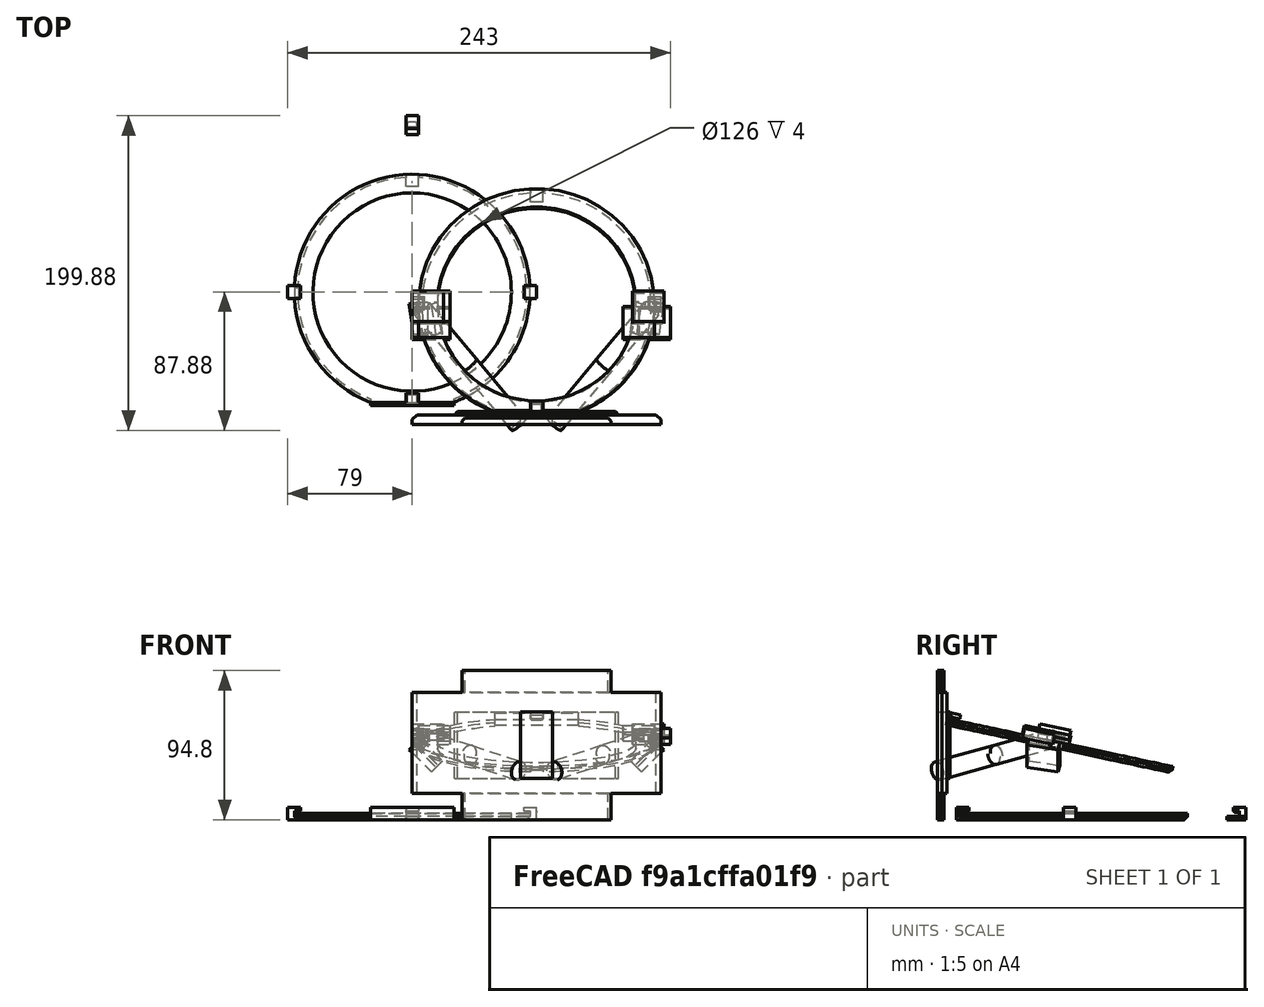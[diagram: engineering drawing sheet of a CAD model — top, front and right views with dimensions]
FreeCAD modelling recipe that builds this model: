
FCSTD DOCUMENT  (FreeCAD 0.19R0.19.2)
Label: waferHolder_024
License: All rights reserved
LicenseURL: http://en.wikipedia.org/wiki/All_rights_reserved
objects: Part::Box×55, Part::Chamfer×36, Part::MultiFuse×21, Part::Cylinder×16, Part::Cut×14, Sketcher::SketchObject×9, Part::Extrusion×9, Part::Fuse×4, Part::Mirroring×2, App::MeasureDistance×1
note: 166 computed .brp shape members not serialized (recipe doc carries the construction recipe); baked Part::Feature solids carry a one-line shape summary decoded from their .brp

FEATURE [Part::Box] Box003  label="bitHolderTop"
  AttacherType = Attacher::AttachEngine3D
  Height = 2
  Length = 8
  Placement = pos=(-4,100,0) rot=(0,0,1;0rad)
  Width = 12
FEATURE [Part::Box] Box008  label="holderBitLeft003"
  AttacherType = Attacher::AttachEngine3D
  Height = 2
  Length = 8
  Placement = pos=(-4,71,2) rot=(0,0,1;0rad)
  Width = 8
FEATURE [Part::Box] Box009  label="bitHolderTopCutout001"
  AttacherType = Attacher::AttachEngine3D
  Height = 4
  Length = 8
  Placement = pos=(-4,67,-2) rot=(0,0,1;0rad)
  Width = 12
FEATURE [Sketcher::SketchObject] Sketch002
  FullyConstrained = true
  sketch-geometry (3):
    g0: Circle CenterX=-3.1415e-12 CenterY=5.6243e-12 CenterZ=0 NormalX=0 NormalY=0 NormalZ=1 AngleXU=0 Radius=63
    g1: ArcOfCircle CenterX=-3.1415e-12 CenterY=5.6243e-12 CenterZ=0 NormalX=0 NormalY=0 NormalZ=1 AngleXU=0 Radius=74.8482 StartAngle=5.07429 EndAngle=10.6337
    g2: LineSegment StartX=-26.5 StartY=-70.0001 StartZ=0 EndX=26.5 EndY=-70.0001 EndZ=0
  constraints (6):
    c: Block(g0)
    c: Coincident(g1,g0)
    c: Block(g1)
    c: Coincident(g2,g1)
    c: Coincident(g2,g1)
    c: Horizontal(g2)
FEATURE [Part::Extrusion] Extrude002  label="mainHolderRing003"
  Base = -> Sketch002
  Dir = (0,0,1)
  DirMode = 2
  FaceMakerClass = Part::FaceMakerBullseye
  LengthFwd = 4
  LengthRev = 0
  Solid = true
  Symmetric = false
FEATURE [Part::Chamfer] Chamfer001
  Base = -> Extrude002
  Edges = 1 edges r=2: [Edge3]
FEATURE [Part::Cut] Cut002  label="mainHolderRing004"
  Base = -> Chamfer001
  Tool = -> Box009
FEATURE [Part::Cut] Cut003  label="bitHolderTop001"
  Base = -> Box008
  Tool = -> Cut002
FEATURE [Part::Box] Box010  label="holderBitLeft004"
  AttacherType = Attacher::AttachEngine3D
  Height = 2
  Length = 8
  Placement = pos=(-4,71,2) rot=(0,0,1;0rad)
  Width = 8
FEATURE [Part::Box] Box011  label="bitHolderTopCutout002"
  AttacherType = Attacher::AttachEngine3D
  Height = 4
  Length = 8
  Placement = pos=(-4,67,-2) rot=(0,0,1;0rad)
  Width = 12
FEATURE [Sketcher::SketchObject] Sketch003
  FullyConstrained = true
  sketch-geometry (3):
    g0: Circle CenterX=-3.1415e-12 CenterY=5.6243e-12 CenterZ=0 NormalX=0 NormalY=0 NormalZ=1 AngleXU=0 Radius=63
    g1: ArcOfCircle CenterX=-3.1415e-12 CenterY=5.6243e-12 CenterZ=0 NormalX=0 NormalY=0 NormalZ=1 AngleXU=0 Radius=74.8482 StartAngle=5.07429 EndAngle=10.6337
    g2: LineSegment StartX=-26.5 StartY=-70.0001 StartZ=0 EndX=26.5 EndY=-70.0001 EndZ=0
  constraints (6):
    c: Block(g0)
    c: Coincident(g1,g0)
    c: Block(g1)
    c: Coincident(g2,g1)
    c: Coincident(g2,g1)
    c: Horizontal(g2)
FEATURE [Part::Extrusion] Extrude003  label="mainHolderRing006"
  Base = -> Sketch003
  Dir = (0,0,1)
  DirMode = 2
  FaceMakerClass = Part::FaceMakerBullseye
  LengthFwd = 4
  LengthRev = 0
  Solid = true
  Symmetric = false
FEATURE [Part::Chamfer] Chamfer002
  Base = -> Extrude003
  Edges = 1 edges r=2: [Edge3]
FEATURE [Part::Cut] Cut005  label="mainHolderRing005"
  Base = -> Chamfer002
  Tool = -> Box011
FEATURE [Part::Cut] Cut004  label="bitHolderTop002"
  Base = -> Box010
  Placement = pos=(0,0,2) rot=(0,0,1;0rad)
  Tool = -> Cut005
FEATURE [Part::Box] Box012  label="holderBitLeft005"
  AttacherType = Attacher::AttachEngine3D
  Height = 2
  Length = 8
  Placement = pos=(-4,71,2) rot=(0,0,1;0rad)
  Width = 8
FEATURE [Part::Box] Box013  label="bitHolderTopCutout003"
  AttacherType = Attacher::AttachEngine3D
  Height = 4
  Length = 8
  Placement = pos=(-4,67,-2) rot=(0,0,1;0rad)
  Width = 12
FEATURE [Sketcher::SketchObject] Sketch004
  FullyConstrained = true
  sketch-geometry (3):
    g0: Circle CenterX=-3.1415e-12 CenterY=5.6243e-12 CenterZ=0 NormalX=0 NormalY=0 NormalZ=1 AngleXU=0 Radius=63
    g1: ArcOfCircle CenterX=-3.1415e-12 CenterY=5.6243e-12 CenterZ=0 NormalX=0 NormalY=0 NormalZ=1 AngleXU=0 Radius=74.8482 StartAngle=5.07429 EndAngle=10.6337
    g2: LineSegment StartX=-26.5 StartY=-70.0001 StartZ=0 EndX=26.5 EndY=-70.0001 EndZ=0
  constraints (6):
    c: Block(g0)
    c: Coincident(g1,g0)
    c: Block(g1)
    c: Coincident(g2,g1)
    c: Coincident(g2,g1)
    c: Horizontal(g2)
FEATURE [Part::Extrusion] Extrude004  label="mainHolderRing008"
  Base = -> Sketch004
  Dir = (0,0,1)
  DirMode = 2
  FaceMakerClass = Part::FaceMakerBullseye
  LengthFwd = 4
  LengthRev = 0
  Solid = true
  Symmetric = false
FEATURE [Part::Chamfer] Chamfer003
  Base = -> Extrude004
  Edges = 1 edges r=2: [Edge3]
FEATURE [Part::Cut] Cut007  label="mainHolderRing007"
  Base = -> Chamfer003
  Tool = -> Box013
FEATURE [Part::Cut] Cut006  label="bitHolderTop003"
  Base = -> Box012
  Placement = pos=(0,0,4) rot=(0,0,1;0rad)
  Tool = -> Cut007
FEATURE [Part::Box] Box014  label="bitHoldertop006"
  AttacherType = Attacher::AttachEngine3D
  Height = 3.4
  Length = 8
  Placement = pos=(-4,71,4.6) rot=(0,0,1;0rad)
  Width = 8
FEATURE [Part::MultiFuse] Fusion001  label="holderTop"
  Placement = pos=(0,33,0) rot=(0,0,1;0rad)
  Shapes = -> [Cut003,Cut004,Cut006,Box014]
FEATURE [Part::Chamfer] Chamfer004
  Base = -> Fusion001
  Edges = 1 edges r=1: [Edge16]
FEATURE [Part::Chamfer] Chamfer009
  Base = -> Chamfer004
  Edges = 1 edges r=1: [Edge1]
FEATURE [Part::Chamfer] Chamfer010
  Base = -> Chamfer009
  Edges = 1 edges r=1: [Edge32]
FEATURE [Part::Box] Box018  label="base001"
  AttacherType = Attacher::AttachEngine3D
  Height = 64.44
  Length = 158
  Placement = pos=(0,-84,16.6) rot=(0,0,1;0rad)
  Width = 6
FEATURE [Part::Box] Box019  label="base002"
  AttacherType = Attacher::AttachEngine3D
  Height = 94.8
  Length = 94.8
  Placement = pos=(31.6,-84,0) rot=(0,0,1;0rad)
  Width = 4
FEATURE [Part::Box] Box020  label="base003"
  AttacherType = Attacher::AttachEngine3D
  Height = 42.44
  Length = 104.28
  Placement = pos=(26.86,-84,26.18) rot=(0,0,1;0rad)
  Width = 8
FEATURE [Part::Chamfer] Chamfer014
  Base = -> Box018
  Edges = 1 edges r=3: [Edge3]
FEATURE [Part::Chamfer] Chamfer015
  Base = -> Chamfer014
  Edges = 1 edges r=3: [Edge15]
FEATURE [Part::Chamfer] Chamfer016
  Base = -> Box019
  Edges = 1 edges r=2: [Edge3]
FEATURE [Part::Chamfer] Chamfer017
  Base = -> Box020
  Edges = 1 edges r=2: [Edge3]
FEATURE [Part::Chamfer] Chamfer018
  Base = -> Chamfer016
  Edges = 1 edges r=2: [Edge15]
FEATURE [Part::Chamfer] Chamfer019
  Base = -> Chamfer017
  Edges = 1 edges r=2: [Edge15]
FEATURE [Part::MultiFuse] Fusion002  label="base004"
  Shapes = -> [Chamfer015,Chamfer018,Chamfer019]
FEATURE [Part::Box] Box021  label="holderBitLeft006"
  AttacherType = Attacher::AttachEngine3D
  Height = 4
  Length = 6
  Placement = pos=(-79,-4,0) rot=(0,0,1;0rad)
  Width = 8
FEATURE [Part::Box] Box022  label="holderBitright003"
  AttacherType = Attacher::AttachEngine3D
  Height = 4
  Length = 6
  Placement = pos=(73,-4,0) rot=(0,0,1;0rad)
  Width = 8
FEATURE [Part::Box] Box023  label="holderBitLeft007"
  AttacherType = Attacher::AttachEngine3D
  Height = 3.4
  Length = 8
  Placement = pos=(-79,-4,4.6) rot=(0,0,1;0rad)
  Width = 8
FEATURE [Part::Box] Box024  label="holderBitRight003"
  AttacherType = Attacher::AttachEngine3D
  Height = 3.4
  Length = 8
  Placement = pos=(71,-4,4.6) rot=(0,0,1;0rad)
  Width = 8
FEATURE [Sketcher::SketchObject] Sketch005
  FullyConstrained = true
  sketch-geometry (3):
    g0: Circle CenterX=-3.1415e-12 CenterY=5.6243e-12 CenterZ=0 NormalX=0 NormalY=0 NormalZ=1 AngleXU=0 Radius=63
    g1: ArcOfCircle CenterX=-3.1415e-12 CenterY=5.6243e-12 CenterZ=0 NormalX=0 NormalY=0 NormalZ=1 AngleXU=0 Radius=74.8482 StartAngle=5.07429 EndAngle=10.6337
    g2: LineSegment StartX=-26.5 StartY=-70.0001 StartZ=0 EndX=26.5 EndY=-70.0001 EndZ=0
  constraints (6):
    c: Block(g0)
    c: Coincident(g1,g0)
    c: Block(g1)
    c: Coincident(g2,g1)
    c: Coincident(g2,g1)
    c: Horizontal(g2)
FEATURE [Part::Box] Box025  label="holderBitLeft008"
  AttacherType = Attacher::AttachEngine3D
  Height = 4
  Length = 8
  Placement = pos=(-79,-4,0) rot=(0,0,1;0rad)
  Width = 8
FEATURE [Part::Box] Box026  label="bitHolderTopCutout004"
  AttacherType = Attacher::AttachEngine3D
  Height = 4
  Length = 8
  Placement = pos=(-4,67,-2) rot=(0,0,1;0rad)
  Width = 12
FEATURE [Part::Extrusion] Extrude006  label="mainHolderRing010"
  Base = -> Sketch005
  Dir = (0,0,1)
  DirMode = 2
  FaceMakerClass = Part::FaceMakerBullseye
  LengthFwd = 4
  LengthRev = 0
  Solid = true
  Symmetric = false
FEATURE [Part::Box] Box027  label="holderBitRight004"
  AttacherType = Attacher::AttachEngine3D
  Height = 4
  Length = 8
  Placement = pos=(71,-4,0) rot=(0,0,1;0rad)
  Width = 8
FEATURE [Part::Chamfer] Chamfer020
  Base = -> Extrude006
  Edges = 1 edges r=2: [Edge3]
FEATURE [Part::Cut] Cut008  label="mainHolderRing011"
  Base = -> Chamfer020
  Tool = -> Box026
FEATURE [Part::MultiFuse] Fusion004  label="holders001"
  Shapes = -> [Box021,Box022]
FEATURE [Sketcher::SketchObject] Sketch006
  FullyConstrained = true
  sketch-geometry (3):
    g0: Circle CenterX=-3.1415e-12 CenterY=5.6243e-12 CenterZ=0 NormalX=0 NormalY=0 NormalZ=1 AngleXU=0 Radius=63
    g1: ArcOfCircle CenterX=-3.1415e-12 CenterY=5.6243e-12 CenterZ=0 NormalX=0 NormalY=0 NormalZ=1 AngleXU=0 Radius=74.8482 StartAngle=5.07429 EndAngle=10.6337
    g2: LineSegment StartX=-26.5 StartY=-70.0001 StartZ=0 EndX=26.5 EndY=-70.0001 EndZ=0
  constraints (6):
    c: Block(g0)
    c: Coincident(g1,g0)
    c: Block(g1)
    c: Coincident(g2,g1)
    c: Coincident(g2,g1)
    c: Horizontal(g2)
FEATURE [Part::Extrusion] Extrude005  label="mainHolderRing009"
  Base = -> Sketch006
  Dir = (0,0,1)
  DirMode = 2
  FaceMakerClass = Part::FaceMakerBullseye
  LengthFwd = 4
  LengthRev = 0
  Solid = true
  Symmetric = false
FEATURE [Part::Cut] Cut009  label="leftAndRightHolderBits001"
  Base = -> Fusion004
  Placement = pos=(0,0,4) rot=(0,0,1;0rad)
  Tool = -> Extrude005
FEATURE [Part::Chamfer] Chamfer021
  Base = -> Box023
  Edges = 1 edges r=1: [Edge8]
FEATURE [Part::Chamfer] Chamfer022
  Base = -> Box024
  Edges = 1 edges r=1: [Edge4]
FEATURE [Part::Chamfer] Chamfer023
  Base = -> Chamfer022
  Edges = 1 edges r=1: [Edge13]
FEATURE [Part::Chamfer] Chamfer024
  Base = -> Chamfer023
  Edges = 1 edges r=1: [Edge5]
FEATURE [Part::Box] Box028  label="holderBottom004"
  AttacherType = Attacher::AttachEngine3D
  Height = 4
  Length = 53
  Placement = pos=(-26.5,-72,0) rot=(0,0,1;0rad)
  Width = 4.5
FEATURE [Part::Chamfer] Chamfer025
  Base = -> Chamfer021
  Edges = 1 edges r=1: [Edge5]
FEATURE [Part::Chamfer] Chamfer026
  Base = -> Chamfer025
  Edges = 1 edges r=1: [Edge16]
FEATURE [Part::Box] Box029  label="holderBottom006"
  AttacherType = Attacher::AttachEngine3D
  Height = 4
  Length = 53
  Placement = pos=(-26.5,-72,4) rot=(0,0,1;0rad)
  Width = 2
FEATURE [Part::Box] Box030  label="holderBottom007"
  AttacherType = Attacher::AttachEngine3D
  Height = 3.4
  Length = 8
  Placement = pos=(-4,-72,4.6) rot=(0,0,1;0rad)
  Width = 8
FEATURE [Part::Chamfer] Chamfer027  label="holderBottom005"
  Base = -> Box030
  Edges = 3 edges r=1: [Edge4,Edge8,Edge11]
FEATURE [Part::MultiFuse] Fusion005  label="removeRingHolder"
  Placement = pos=(79,-8.35,45.4) rot=(1,0,0;6.07375rad)
  Shapes = -> [Box025,Box027,Cut008,Cut009,Chamfer024,Chamfer026,Box028,Box029,Chamfer027]
FEATURE [Part::Box] Box017  label="holderBottom002"
  AttacherType = Attacher::AttachEngine3D
  Height = 3.4
  Length = 8
  Placement = pos=(-4,-72,4.6) rot=(0,0,1;0rad)
  Width = 8
FEATURE [Part::Chamfer] Chamfer013  label="holderBottom003"
  Base = -> Box017
  Edges = 3 edges r=1: [Edge4,Edge8,Edge11]
FEATURE [Part::Box] Box016  label="holderBottom001"
  AttacherType = Attacher::AttachEngine3D
  Height = 4
  Length = 53
  Placement = pos=(-26.5,-72,4) rot=(0,0,1;0rad)
  Width = 2
FEATURE [Part::Box] Box015  label="holderBottom"
  AttacherType = Attacher::AttachEngine3D
  Height = 4
  Length = 53
  Placement = pos=(-26.5,-72,0) rot=(0,0,1;0rad)
  Width = 4.5
FEATURE [Part::Box] Box006  label="holderBitLeft002"
  AttacherType = Attacher::AttachEngine3D
  Height = 3.4
  Length = 8
  Placement = pos=(-79,-4,4.6) rot=(0,0,1;0rad)
  Width = 8
FEATURE [Part::Chamfer] Chamfer005
  Base = -> Box006
  Edges = 1 edges r=1: [Edge8]
FEATURE [Part::Chamfer] Chamfer011
  Base = -> Chamfer005
  Edges = 1 edges r=1: [Edge5]
FEATURE [Part::Chamfer] Chamfer012
  Base = -> Chamfer011
  Edges = 1 edges r=1: [Edge16]
FEATURE [Part::Box] Box007  label="holderBitRight002"
  AttacherType = Attacher::AttachEngine3D
  Height = 3.4
  Length = 8
  Placement = pos=(71,-4,4.6) rot=(0,0,1;0rad)
  Width = 8
FEATURE [Part::Chamfer] Chamfer006
  Base = -> Box007
  Edges = 1 edges r=1: [Edge4]
FEATURE [Part::Chamfer] Chamfer007
  Base = -> Chamfer006
  Edges = 1 edges r=1: [Edge13]
FEATURE [Part::Chamfer] Chamfer008
  Base = -> Chamfer007
  Edges = 1 edges r=1: [Edge5]
FEATURE [Sketcher::SketchObject] Sketch001
  FullyConstrained = true
  sketch-geometry (3):
    g0: Circle CenterX=-3.1415e-12 CenterY=5.6243e-12 CenterZ=0 NormalX=0 NormalY=0 NormalZ=1 AngleXU=0 Radius=63
    g1: ArcOfCircle CenterX=-3.1415e-12 CenterY=5.6243e-12 CenterZ=0 NormalX=0 NormalY=0 NormalZ=1 AngleXU=0 Radius=74.8482 StartAngle=5.07429 EndAngle=10.6337
    g2: LineSegment StartX=-26.5 StartY=-70.0001 StartZ=0 EndX=26.5 EndY=-70.0001 EndZ=0
  constraints (6):
    c: Block(g0)
    c: Coincident(g1,g0)
    c: Block(g1)
    c: Coincident(g2,g1)
    c: Coincident(g2,g1)
    c: Horizontal(g2)
FEATURE [Part::Extrusion] Extrude001  label="mainHolderRing002"
  Base = -> Sketch001
  Dir = (0,0,1)
  DirMode = 2
  FaceMakerClass = Part::FaceMakerBullseye
  LengthFwd = 4
  LengthRev = 0
  Solid = true
  Symmetric = false
FEATURE [Part::Box] Box005  label="holderBitright002"
  AttacherType = Attacher::AttachEngine3D
  Height = 4
  Length = 6
  Placement = pos=(73,-4,0) rot=(0,0,1;0rad)
  Width = 8
FEATURE [Part::Box] Box004  label="holderBitLeft001"
  AttacherType = Attacher::AttachEngine3D
  Height = 4
  Length = 6
  Placement = pos=(-79,-4,0) rot=(0,0,1;0rad)
  Width = 8
FEATURE [Part::MultiFuse] Fusion  label="holders"
  Shapes = -> [Box004,Box005]
FEATURE [Part::Cut] Cut001  label="leftAndRightHolderBits"
  Base = -> Fusion
  Placement = pos=(0,0,4) rot=(0,0,1;0rad)
  Tool = -> Extrude001
FEATURE [Part::Box] Box001  label="bitHolderTopCutout"
  AttacherType = Attacher::AttachEngine3D
  Height = 4
  Length = 8
  Placement = pos=(-4,67,-2) rot=(0,0,1;0rad)
  Width = 12
FEATURE [Sketcher::SketchObject] Sketch
  FullyConstrained = true
  sketch-geometry (3):
    g0: Circle CenterX=-3.1415e-12 CenterY=5.6243e-12 CenterZ=0 NormalX=0 NormalY=0 NormalZ=1 AngleXU=0 Radius=63
    g1: ArcOfCircle CenterX=-3.1415e-12 CenterY=5.6243e-12 CenterZ=0 NormalX=0 NormalY=0 NormalZ=1 AngleXU=0 Radius=74.8482 StartAngle=5.07429 EndAngle=10.6337
    g2: LineSegment StartX=-26.5 StartY=-70.0001 StartZ=0 EndX=26.5 EndY=-70.0001 EndZ=0
  constraints (6):
    c: Block(g0)
    c: Coincident(g1,g0)
    c: Block(g1)
    c: Coincident(g2,g1)
    c: Coincident(g2,g1)
    c: Horizontal(g2)
FEATURE [Part::Extrusion] Extrude  label="mainHolderRing"
  Base = -> Sketch
  Dir = (0,0,1)
  DirMode = 2
  FaceMakerClass = Part::FaceMakerBullseye
  LengthFwd = 4
  LengthRev = 0
  Solid = true
  Symmetric = false
FEATURE [Part::Chamfer] Chamfer
  Base = -> Extrude
  Edges = 1 edges r=2: [Edge3]
FEATURE [Part::Cut] Cut  label="mainHolderRing001"
  Base = -> Chamfer
  Tool = -> Box001
FEATURE [Part::Box] Box002  label="holderBitRight"
  AttacherType = Attacher::AttachEngine3D
  Height = 4
  Length = 8
  Placement = pos=(71,-4,0) rot=(0,0,1;0rad)
  Width = 8
FEATURE [Part::Box] Box  label="holderBitLeft"
  AttacherType = Attacher::AttachEngine3D
  Height = 4
  Length = 8
  Placement = pos=(-79,-4,0) rot=(0,0,1;0rad)
  Width = 8
FEATURE [Part::MultiFuse] Fusion003  label="ringHolder"
  Shapes = -> [Box,Box002,Cut,Cut001,Chamfer008,Chamfer012,Box015,Box016,Chamfer013]
FEATURE [Part::Cylinder] Cylinder
  Angle = 360
  AttacherType = Attacher::AttachEngine3D
  Height = 50
  Placement = pos=(34.86,-30,47.4) rot=(1,0,0;1.5708rad)
  Radius = 6
FEATURE [Part::Box] Box031  label="base005"
  AttacherType = Attacher::AttachEngine3D
  Height = 42.44
  Length = 20.28
  Placement = pos=(68.86,-84,26.18) rot=(0,0,1;0rad)
  Width = 8
FEATURE [Part::Cylinder] Cylinder001
  Angle = 360
  AttacherType = Attacher::AttachEngine3D
  Height = 50
  Placement = pos=(34.86,-30,47.4) rot=(1,0,0;1.5708rad)
  Radius = 6
FEATURE [Part::MultiFuse] Fusion006
  Placement = pos=(0,0,0) rot=(1,0,0;0.20944rad)
  Shapes = -> [Cylinder001,Cylinder]
FEATURE [Part::Cylinder] Cylinder002
  Angle = 360
  AttacherType = Attacher::AttachEngine3D
  Height = 50
  Placement = pos=(34.86,-30,47.4) rot=(1,0,0;1.5708rad)
  Radius = 6
FEATURE [Part::Cylinder] Cylinder003
  Angle = 360
  AttacherType = Attacher::AttachEngine3D
  Height = 50
  Placement = pos=(34.86,-30,47.4) rot=(1,0,0;1.5708rad)
  Radius = 6
FEATURE [Part::MultiFuse] Fusion007
  Placement = pos=(0,0,0) rot=(1,0,0;0.20944rad)
  Shapes = -> [Cylinder003,Cylinder002]
FEATURE [Part::MultiFuse] Fusion008
  Placement = pos=(-44.06,-5,11.27) rot=(0,0,1;0.698132rad)
  Shapes = -> [Fusion007,Fusion006]
FEATURE [App::MeasureDistance] Distance  label="Distance: 0.65 mm"
  Distance = 0.654413
  P1 = (68.86,-76,67.959)
  P2 = (68.8586,-76,68.6134)
FEATURE [Part::Cylinder] Cylinder004
  Angle = 360
  AttacherType = Attacher::AttachEngine3D
  Height = 50
  Placement = pos=(34.86,-30,47.4) rot=(1,0,0;1.5708rad)
  Radius = 6
FEATURE [Part::Cylinder] Cylinder005
  Angle = 360
  AttacherType = Attacher::AttachEngine3D
  Height = 50
  Placement = pos=(34.86,-30,47.4) rot=(1,0,0;1.5708rad)
  Radius = 6
FEATURE [Part::MultiFuse] Fusion010
  Placement = pos=(0,0,0) rot=(1,0,0;0.20944rad)
  Shapes = -> [Cylinder005,Cylinder004]
FEATURE [Part::Cylinder] Cylinder006
  Angle = 360
  AttacherType = Attacher::AttachEngine3D
  Height = 50
  Placement = pos=(34.86,-30,47.4) rot=(1,0,0;1.5708rad)
  Radius = 6
FEATURE [Part::Cylinder] Cylinder007
  Angle = 360
  AttacherType = Attacher::AttachEngine3D
  Height = 50
  Placement = pos=(34.86,-30,47.4) rot=(1,0,0;1.5708rad)
  Radius = 6
FEATURE [Part::MultiFuse] Fusion009
  Placement = pos=(0,0,0) rot=(1,0,0;0.20944rad)
  Shapes = -> [Cylinder007,Cylinder006]
FEATURE [Part::MultiFuse] Fusion011
  Placement = pos=(-14,-40.82,1.35) rot=(0,0,1;0.698132rad)
  Shapes = -> [Fusion009,Fusion010]
FEATURE [Part::Fuse] Fusion012
  Base = -> Fusion008
  Placement = pos=(-1.7,2,0) rot=(0,0,1;0rad)
  Tool = -> Fusion011
FEATURE [Part::Mirroring] Part__Mirroring  label="rightStrut"
  Base = (0,0,0)
  Normal = (1,0,0)
  Placement = pos=(158,0,0) rot=(0,0,1;0rad)
  Source = -> Fusion012
FEATURE [Part::Box] Box032  label="removeStrutLeft"
  AttacherType = Attacher::AttachEngine3D
  Height = 6
  Length = 20
  Placement = pos=(4,-30.1,54.1) rot=(1,0,0;6.07375rad)
  Width = 20
FEATURE [Part::Box] Box033  label="reoveStrustRight"
  AttacherType = Attacher::AttachEngine3D
  Height = 6
  Length = 20
  Placement = pos=(134,-30.1,54.1) rot=(-1,0,0;0.20944rad)
  Width = 20
FEATURE [Part::Box] Box034  label="removeStrutLeft001"
  AttacherType = Attacher::AttachEngine3D
  Height = 6
  Length = 20
  Placement = pos=(4,-30.1,54.1) rot=(-1,0,0;0.20944rad)
  Width = 20
FEATURE [Part::Box] Box035  label="removeStrutLeft002"
  AttacherType = Attacher::AttachEngine3D
  Height = 6
  Length = 20
  Placement = pos=(4,-30.1,54.1) rot=(-1,0,0;0.20944rad)
  Width = 20
FEATURE [Part::Fuse] Fusion013
  Base = -> Box034
  Placement = pos=(-40,3,12) rot=(0,1,0;0.785398rad)
  Tool = -> Box035
FEATURE [Part::Mirroring] Part__Mirroring001  label="removeFromRightStrust002"
  Base = (0,0,0)
  Normal = (1,0,0)
  Placement = pos=(158,0,0) rot=(0,0,1;0rad)
  Source = -> Fusion013
FEATURE [Part::Box] Box036  label="reoveStrustRight001"
  AttacherType = Attacher::AttachEngine3D
  Height = 6
  Length = 20
  Placement = pos=(144,-30.1,52.1) rot=(-1,0,0;0.20944rad)
  Width = 20
FEATURE [Part::Box] Box037  label="reoveStrustLeft002"
  AttacherType = Attacher::AttachEngine3D
  Height = 6
  Length = 20
  Placement = pos=(0,-30.1,52.1) rot=(-1,0,0;0.20944rad)
  Width = 20
FEATURE [Sketcher::SketchObject] Sketch007
  FullyConstrained = true
  sketch-geometry (3):
    g0: Circle CenterX=-3.1415e-12 CenterY=5.6243e-12 CenterZ=0 NormalX=0 NormalY=0 NormalZ=1 AngleXU=0 Radius=63
    g1: ArcOfCircle CenterX=-3.1415e-12 CenterY=5.6243e-12 CenterZ=0 NormalX=0 NormalY=0 NormalZ=1 AngleXU=0 Radius=74.8482 StartAngle=5.07429 EndAngle=10.6337
    g2: LineSegment StartX=-26.5 StartY=-70.0001 StartZ=0 EndX=26.5 EndY=-70.0001 EndZ=0
  constraints (6):
    c: Block(g0)
    c: Coincident(g1,g0)
    c: Block(g1)
    c: Coincident(g2,g1)
    c: Coincident(g2,g1)
    c: Horizontal(g2)
FEATURE [Part::Box] Box038  label="holderBitLeft009"
  AttacherType = Attacher::AttachEngine3D
  Height = 4
  Length = 6
  Placement = pos=(-79,-4,0) rot=(0,0,1;0rad)
  Width = 8
FEATURE [Part::Box] Box039  label="holderBitright004"
  AttacherType = Attacher::AttachEngine3D
  Height = 4
  Length = 6
  Placement = pos=(73,-4,0) rot=(0,0,1;0rad)
  Width = 8
FEATURE [Part::Box] Box040  label="holderBitLeft010"
  AttacherType = Attacher::AttachEngine3D
  Height = 3.4
  Length = 8
  Placement = pos=(-79,-4,4.6) rot=(0,0,1;0rad)
  Width = 8
FEATURE [Part::Box] Box041  label="holderBitRight005"
  AttacherType = Attacher::AttachEngine3D
  Height = 3.4
  Length = 8
  Placement = pos=(71,-4,4.6) rot=(0,0,1;0rad)
  Width = 8
FEATURE [Part::Extrusion] Extrude008  label="mainHolderRing013"
  Base = -> Sketch007
  Dir = (0,0,1)
  DirMode = 2
  FaceMakerClass = Part::FaceMakerBullseye
  LengthFwd = 4
  LengthRev = 0
  Solid = true
  Symmetric = false
FEATURE [Part::Box] Box042  label="holderBitRight006"
  AttacherType = Attacher::AttachEngine3D
  Height = 4
  Length = 8
  Placement = pos=(71,-4,0) rot=(0,0,1;0rad)
  Width = 8
FEATURE [Part::Box] Box043  label="holderBottom008"
  AttacherType = Attacher::AttachEngine3D
  Height = 4
  Length = 53
  Placement = pos=(-26.5,-72,0) rot=(0,0,1;0rad)
  Width = 4.5
FEATURE [Part::Box] Box044  label="holderBottom009"
  AttacherType = Attacher::AttachEngine3D
  Height = 4
  Length = 53
  Placement = pos=(-26.5,-72,4) rot=(0,0,1;0rad)
  Width = 2
FEATURE [Part::Box] Box045  label="holderBottom010"
  AttacherType = Attacher::AttachEngine3D
  Height = 3.4
  Length = 8
  Placement = pos=(-4,-72,4.6) rot=(0,0,1;0rad)
  Width = 8
FEATURE [Part::Box] Box046  label="holderBitLeft011"
  AttacherType = Attacher::AttachEngine3D
  Height = 4
  Length = 8
  Placement = pos=(-79,-4,0) rot=(0,0,1;0rad)
  Width = 8
FEATURE [Part::Box] Box047  label="bitHolderTopCutout005"
  AttacherType = Attacher::AttachEngine3D
  Height = 4
  Length = 8
  Placement = pos=(-4,67,-2) rot=(0,0,1;0rad)
  Width = 12
FEATURE [Part::Chamfer] Chamfer031  label="holderBottom011"
  Base = -> Box045
  Edges = 3 edges r=1: [Edge4,Edge8,Edge11]
FEATURE [Sketcher::SketchObject] Sketch008
  FullyConstrained = true
  sketch-geometry (3):
    g0: Circle CenterX=-3.1415e-12 CenterY=5.6243e-12 CenterZ=0 NormalX=0 NormalY=0 NormalZ=1 AngleXU=0 Radius=63
    g1: ArcOfCircle CenterX=-3.1415e-12 CenterY=5.6243e-12 CenterZ=0 NormalX=0 NormalY=0 NormalZ=1 AngleXU=0 Radius=74.8482 StartAngle=5.07429 EndAngle=10.6337
    g2: LineSegment StartX=-26.5 StartY=-70.0001 StartZ=0 EndX=26.5 EndY=-70.0001 EndZ=0
  constraints (6):
    c: Block(g0)
    c: Coincident(g1,g0)
    c: Block(g1)
    c: Coincident(g2,g1)
    c: Coincident(g2,g1)
    c: Horizontal(g2)
FEATURE [Part::Extrusion] Extrude007  label="mainHolderRing012"
  Base = -> Sketch008
  Dir = (0,0,1)
  DirMode = 2
  FaceMakerClass = Part::FaceMakerBullseye
  LengthFwd = 4
  LengthRev = 0
  Solid = true
  Symmetric = false
FEATURE [Part::Chamfer] Chamfer032
  Base = -> Extrude008
  Edges = 1 edges r=2: [Edge3]
FEATURE [Part::Cut] Cut010  label="mainHolderRing014"
  Base = -> Chamfer032
  Tool = -> Box047
FEATURE [Part::MultiFuse] Fusion015  label="holders002"
  Shapes = -> [Box038,Box039]
FEATURE [Part::Cut] Cut011  label="leftAndRightHolderBits002"
  Base = -> Fusion015
  Placement = pos=(0,0,4) rot=(0,0,1;0rad)
  Tool = -> Extrude007
FEATURE [Part::Chamfer] Chamfer033
  Base = -> Box040
  Edges = 1 edges r=1: [Edge8]
FEATURE [Part::Chamfer] Chamfer029
  Base = -> Chamfer033
  Edges = 1 edges r=1: [Edge5]
FEATURE [Part::Chamfer] Chamfer030
  Base = -> Chamfer029
  Edges = 1 edges r=1: [Edge16]
FEATURE [Part::Chamfer] Chamfer034
  Base = -> Box041
  Edges = 1 edges r=1: [Edge4]
FEATURE [Part::Chamfer] Chamfer035
  Base = -> Chamfer034
  Edges = 1 edges r=1: [Edge13]
FEATURE [Part::Chamfer] Chamfer028
  Base = -> Chamfer035
  Edges = 1 edges r=1: [Edge5]
FEATURE [Part::MultiFuse] Fusion014  label="removeRingHolder001"
  Placement = pos=(79,-8.35,45.4) rot=(-1,0,0;0.20944rad)
  Shapes = -> [Box046,Box042,Cut010,Cut011,Chamfer028,Chamfer030,Box043,Box044,Chamfer031]
FEATURE [Part::MultiFuse] Fusion016  label="removeFromStruts"
  Shapes = -> [Box037,Box036]
FEATURE [Part::Cut] Cut012  label="removeFromStruts001"
  Base = -> Fusion016
  Tool = -> Fusion005
FEATURE [Part::Cylinder] Cylinder008
  Angle = 360
  AttacherType = Attacher::AttachEngine3D
  Height = 50
  Placement = pos=(34.86,-30,47.4) rot=(1,0,0;1.5708rad)
  Radius = 6
FEATURE [Part::Cylinder] Cylinder009
  Angle = 360
  AttacherType = Attacher::AttachEngine3D
  Height = 50
  Placement = pos=(34.86,-30,47.4) rot=(1,0,0;1.5708rad)
  Radius = 6
FEATURE [Part::Cylinder] Cylinder010
  Angle = 360
  AttacherType = Attacher::AttachEngine3D
  Height = 50
  Placement = pos=(34.86,-30,47.4) rot=(1,0,0;1.5708rad)
  Radius = 6
FEATURE [Part::MultiFuse] Fusion020
  Placement = pos=(0,0,0) rot=(1,0,0;0.20944rad)
  Shapes = -> [Cylinder010,Cylinder009]
FEATURE [Part::Cylinder] Cylinder011
  Angle = 360
  AttacherType = Attacher::AttachEngine3D
  Height = 50
  Placement = pos=(34.86,-30,47.4) rot=(1,0,0;1.5708rad)
  Radius = 6
FEATURE [Part::MultiFuse] Fusion019
  Placement = pos=(0,0,0) rot=(1,0,0;0.20944rad)
  Shapes = -> [Cylinder011,Cylinder008]
FEATURE [Part::Cylinder] Cylinder012
  Angle = 360
  AttacherType = Attacher::AttachEngine3D
  Height = 50
  Placement = pos=(34.86,-30,47.4) rot=(1,0,0;1.5708rad)
  Radius = 6
FEATURE [Part::Cylinder] Cylinder013
  Angle = 360
  AttacherType = Attacher::AttachEngine3D
  Height = 50
  Placement = pos=(34.86,-30,47.4) rot=(1,0,0;1.5708rad)
  Radius = 6
FEATURE [Part::MultiFuse] Fusion017
  Placement = pos=(0,0,0) rot=(1,0,0;0.20944rad)
  Shapes = -> [Cylinder013,Cylinder012]
FEATURE [Part::MultiFuse] Fusion023
  Placement = pos=(-44.06,-5,11.27) rot=(0,0,1;0.698132rad)
  Shapes = -> [Fusion017,Fusion019]
FEATURE [Part::Cylinder] Cylinder014
  Angle = 360
  AttacherType = Attacher::AttachEngine3D
  Height = 50
  Placement = pos=(34.86,-30,47.4) rot=(1,0,0;1.5708rad)
  Radius = 6
FEATURE [Part::Cylinder] Cylinder015
  Angle = 360
  AttacherType = Attacher::AttachEngine3D
  Height = 50
  Placement = pos=(34.86,-30,47.4) rot=(1,0,0;1.5708rad)
  Radius = 6
FEATURE [Part::MultiFuse] Fusion021
  Placement = pos=(0,0,0) rot=(1,0,0;0.20944rad)
  Shapes = -> [Cylinder015,Cylinder014]
FEATURE [Part::MultiFuse] Fusion022
  Placement = pos=(-14,-40.82,1.35) rot=(0,0,1;0.698132rad)
  Shapes = -> [Fusion020,Fusion021]
FEATURE [Part::Fuse] Fusion018  label="leftstrut"
  Base = -> Fusion023
  Placement = pos=(-1.7,2,0) rot=(0,0,1;0rad)
  Tool = -> Fusion022
FEATURE [Part::Box] Box048  label="removeStrutLeft003"
  AttacherType = Attacher::AttachEngine3D
  Height = 6
  Length = 20
  Placement = pos=(4,-30.1,54.1) rot=(-1,0,0;0.20944rad)
  Width = 20
FEATURE [Part::Box] Box049  label="removeStrutLeft004"
  AttacherType = Attacher::AttachEngine3D
  Height = 6
  Length = 20
  Placement = pos=(4,-30.1,54.1) rot=(-1,0,0;0.20944rad)
  Width = 20
FEATURE [Part::Fuse] Fusion024  label="removeFromLeftStrut002"
  Base = -> Box048
  Placement = pos=(-40,3,12) rot=(0,1,0;0.785398rad)
  Tool = -> Box049
FEATURE [Part::Box] Box050  label="reoveStrustRight002"
  AttacherType = Attacher::AttachEngine3D
  Height = 6
  Length = 20
  Placement = pos=(10,-30.1,52.1) rot=(-1,0,0;0.20944rad)
  Width = 20
FEATURE [Part::Cut] Cut013  label="removeFromStruts003"
  Base = -> Cut012
  Tool = -> Box050
FEATURE [Part::Box] Box051  label="removeStrutLeft005"
  AttacherType = Attacher::AttachEngine3D
  Height = 6
  Length = 20
  Placement = pos=(0,-20.1,54.98) rot=(-1,0,0;0.20944rad)
  Width = 20
FEATURE [Part::Box] Box052  label="removeStrutLeft006"
  AttacherType = Attacher::AttachEngine3D
  Height = 6
  Length = 20
  Placement = pos=(140,-20.1,51.98) rot=(-1,0,0;0.20944rad)
  Width = 20
FEATURE [Part::Box] Box053  label="removeStrutLeft007"
  AttacherType = Attacher::AttachEngine3D
  Height = 6
  Length = 20
  Placement = pos=(4,-20.1,51.98) rot=(-1,0,0;0.20944rad)
  Width = 20
FEATURE [Part::Box] Box054  label="removeStrutLeft008"
  AttacherType = Attacher::AttachEngine3D
  Height = 6
  Length = 20
  Placement = pos=(140,-20.1,54.98) rot=(-1,0,0;0.20944rad)
  Width = 20
